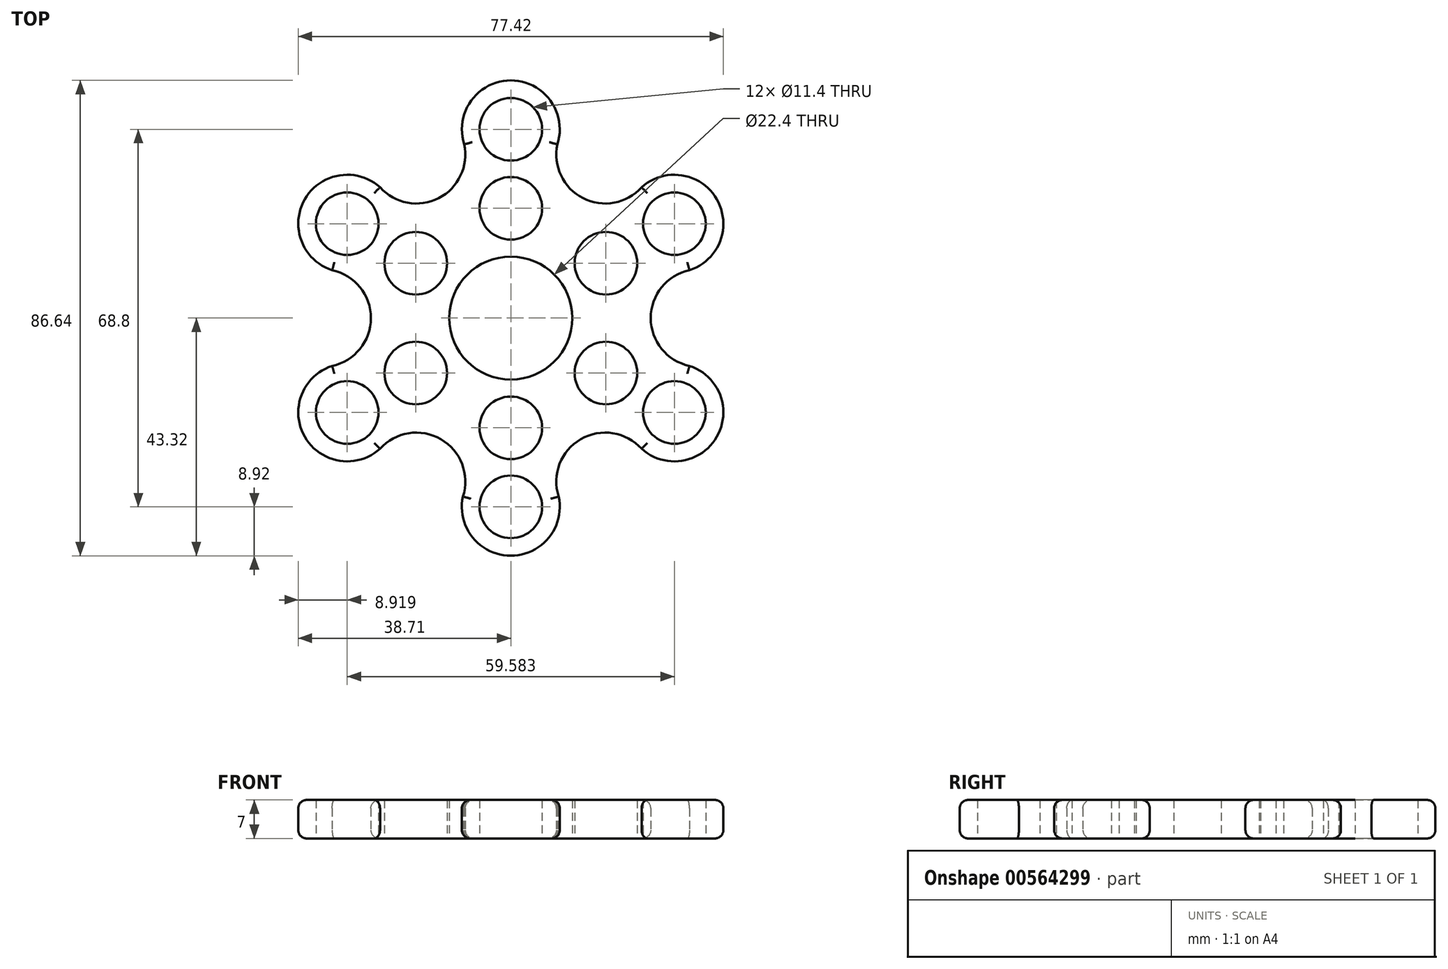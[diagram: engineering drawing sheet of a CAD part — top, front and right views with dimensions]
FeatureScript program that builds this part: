
annotation { "Feature Type Name" : "Feature", "Feature Type Description" : "" }
export const myFeature = defineFeature(function(context is Context, id is Id, definition is map)
    precondition{}
    {
        {
            var Q0;
            Q0=qCreatedBy(makeId("Top.planeOp"),FACE);
            var sketch = newSketch(context, id + "F0", { "sketchPlane" : qUnion([Q0])});
            skCircle(sketch, "E0", {"center": v(0, 0) * mm, "radius": 11.2 * mm});
            skCircle(sketch, "E1", {"center": v(0, 20) * mm, "radius": 5.7 * mm});
            skCircle(sketch, "E2", {"center": v(0, 34.4) * mm, "radius": 5.7 * mm});
            skArc(sketch, "E3", {"start": v(8.48, 31.66) * mm, "mid": v(0, 43.31) * mm, "end": v(-8.48, 31.66) * mm});
            skArc(sketch, "E4.1.0", {"start": v(-23.82, 23.82) * mm, "mid": v(-13.14, 21.85) * mm, "end": v(-8.48, 31.66) * mm});
            skArc(sketch, "E4.2.0", {"start": v(-23.82, 23.82) * mm, "mid": v(-37.51, 21.66) * mm, "end": v(-32.54, 8.72) * mm});
            skArc(sketch, "E4.3.0", {"start": v(-32.54, -8.72) * mm, "mid": v(-25.48, 0) * mm, "end": v(-32.54, 8.72) * mm});
            skArc(sketch, "E4.4.0", {"start": v(-32.54, -8.72) * mm, "mid": v(-37.51, -21.66) * mm, "end": v(-23.82, -23.82) * mm});
            skArc(sketch, "E4.5.0", {"start": v(-8.72, -32.54) * mm, "mid": v(-12.74, -22.07) * mm, "end": v(-23.82, -23.82) * mm});
            skArc(sketch, "E4.6.0", {"start": v(-8.72, -32.54) * mm, "mid": v(0, -43.31) * mm, "end": v(8.72, -32.54) * mm});
            skArc(sketch, "E4.7.0", {"start": v(23.82, -23.82) * mm, "mid": v(12.74, -22.07) * mm, "end": v(8.72, -32.54) * mm});
            skArc(sketch, "E4.8.0", {"start": v(23.82, -23.82) * mm, "mid": v(37.51, -21.66) * mm, "end": v(32.54, -8.72) * mm});
            skArc(sketch, "E4.9.0", {"start": v(32.54, 8.72) * mm, "mid": v(25.48, 0) * mm, "end": v(32.54, -8.72) * mm});
            skArc(sketch, "E4.10.0", {"start": v(32.54, 8.72) * mm, "mid": v(37.51, 21.66) * mm, "end": v(23.82, 23.82) * mm});
            skArc(sketch, "E4.11.0", {"start": v(8.48, 31.66) * mm, "mid": v(13.14, 21.85) * mm, "end": v(23.82, 23.82) * mm});
            skCircle(sketch, "E5.2.0", {"center": v(-29.8, 17.2) * mm, "radius": 5.7 * mm});
            skCircle(sketch, "E5.4.0", {"center": v(-29.8, -17.2) * mm, "radius": 5.7 * mm});
            skCircle(sketch, "E5.6.0", {"center": v(0, -34.4) * mm, "radius": 5.7 * mm});
            skCircle(sketch, "E5.8.0", {"center": v(29.8, -17.2) * mm, "radius": 5.7 * mm});
            skCircle(sketch, "E5.10.0", {"center": v(29.8, 17.2) * mm, "radius": 5.7 * mm});
            skCircle(sketch, "E6.1.0", {"center": v(-17.32, 10) * mm, "radius": 5.7 * mm});
            skCircle(sketch, "E6.2.0", {"center": v(-17.32, -10) * mm, "radius": 5.7 * mm});
            skCircle(sketch, "E6.3.0", {"center": v(0, -20) * mm, "radius": 5.7 * mm});
            skCircle(sketch, "E6.4.0", {"center": v(17.32, -10) * mm, "radius": 5.7 * mm});
            skCircle(sketch, "E6.5.0", {"center": v(17.32, 10) * mm, "radius": 5.7 * mm});
            skSolve(sketch);
        }
        {
            var Q0;
            Q0=makeQuery(id+"F0.imprint","IMPRINT",FACE,{"disambiguationData":[TD([[makeQuery(id+"F0.imprint","IMPRINT",EDGE,{"derivedFrom":sQuery(id+"F0.wireOp",EDGE,"E0")}),-1.0]])]});
            extrude(context, id + "F1", {"entities" : qUnion([Q0]), "depth" : 7 * mm, "offsetDistance" : 25 * mm});
        }
        {
            var Q0;
            Q0=makeQuery(id+"F1.opExtrude","CAP_EDGE",EDGE,{"disambiguationData":[OSD([sQuery(id+"F0.wireOp",EDGE,"E4.1.0")])],"isStart":false});
            var Q1;
            Q1=makeQuery(id+"F1.opExtrude","CAP_EDGE",EDGE,{"disambiguationData":[OSD([sQuery(id+"F0.wireOp",EDGE,"E3")])],"isStart":false});
            var Q2;
            Q2=makeQuery(id+"F1.opExtrude","CAP_EDGE",EDGE,{"disambiguationData":[OSD([sQuery(id+"F0.wireOp",EDGE,"E4.11.0")])],"isStart":false});
            var Q3;
            Q3=makeQuery(id+"F1.opExtrude","CAP_EDGE",EDGE,{"disambiguationData":[OSD([sQuery(id+"F0.wireOp",EDGE,"E4.10.0")])],"isStart":false});
            var Q4;
            Q4=makeQuery(id+"F1.opExtrude","CAP_EDGE",EDGE,{"disambiguationData":[OSD([sQuery(id+"F0.wireOp",EDGE,"E4.9.0")])],"isStart":false});
            var Q5;
            Q5=makeQuery(id+"F1.opExtrude","CAP_EDGE",EDGE,{"disambiguationData":[OSD([sQuery(id+"F0.wireOp",EDGE,"E4.8.0")])],"isStart":false});
            var Q6;
            Q6=makeQuery(id+"F1.opExtrude","CAP_EDGE",EDGE,{"disambiguationData":[OSD([sQuery(id+"F0.wireOp",EDGE,"E4.7.0")])],"isStart":false});
            var Q7;
            Q7=makeQuery(id+"F1.opExtrude","CAP_EDGE",EDGE,{"disambiguationData":[OSD([sQuery(id+"F0.wireOp",EDGE,"E4.6.0")])],"isStart":false});
            var Q8;
            Q8=makeQuery(id+"F1.opExtrude","CAP_EDGE",EDGE,{"disambiguationData":[OSD([sQuery(id+"F0.wireOp",EDGE,"E4.5.0")])],"isStart":false});
            var Q9;
            Q9=makeQuery(id+"F1.opExtrude","CAP_EDGE",EDGE,{"disambiguationData":[OSD([sQuery(id+"F0.wireOp",EDGE,"E4.4.0")])],"isStart":false});
            var Q10;
            Q10=makeQuery(id+"F1.opExtrude","CAP_EDGE",EDGE,{"disambiguationData":[OSD([sQuery(id+"F0.wireOp",EDGE,"E4.3.0")])],"isStart":false});
            var Q11;
            Q11=makeQuery(id+"F1.opExtrude","CAP_EDGE",EDGE,{"disambiguationData":[OSD([sQuery(id+"F0.wireOp",EDGE,"E4.2.0")])],"isStart":false});
            fillet(context, id + "F2", {"entities" : qUnion([Q0, Q1, Q2, Q3, Q4, Q5, Q6, Q7, Q8, Q9, Q10, Q11]), "radius" : 1.5 * mm, "tangentPropagation" : true, "allowEdgeOverflow" : false});
        }
        {
            var Q0;
            Q0=makeQuery(id+"F1.opExtrude","CAP_EDGE",EDGE,{"disambiguationData":[OSD([sQuery(id+"F0.wireOp",EDGE,"E4.4.0")])],"isStart":true});
            var Q1;
            Q1=makeQuery(id+"F1.opExtrude","CAP_EDGE",EDGE,{"disambiguationData":[OSD([sQuery(id+"F0.wireOp",EDGE,"E4.5.0")])],"isStart":true});
            var Q2;
            Q2=makeQuery(id+"F1.opExtrude","CAP_EDGE",EDGE,{"disambiguationData":[OSD([sQuery(id+"F0.wireOp",EDGE,"E4.6.0")])],"isStart":true});
            var Q3;
            Q3=makeQuery(id+"F1.opExtrude","CAP_EDGE",EDGE,{"disambiguationData":[OSD([sQuery(id+"F0.wireOp",EDGE,"E4.7.0")])],"isStart":true});
            var Q4;
            Q4=makeQuery(id+"F1.opExtrude","CAP_EDGE",EDGE,{"disambiguationData":[OSD([sQuery(id+"F0.wireOp",EDGE,"E4.8.0")])],"isStart":true});
            var Q5;
            Q5=makeQuery(id+"F1.opExtrude","CAP_EDGE",EDGE,{"disambiguationData":[OSD([sQuery(id+"F0.wireOp",EDGE,"E4.9.0")])],"isStart":true});
            var Q6;
            Q6=makeQuery(id+"F1.opExtrude","CAP_EDGE",EDGE,{"disambiguationData":[OSD([sQuery(id+"F0.wireOp",EDGE,"E4.10.0")])],"isStart":true});
            var Q7;
            Q7=makeQuery(id+"F1.opExtrude","CAP_EDGE",EDGE,{"disambiguationData":[OSD([sQuery(id+"F0.wireOp",EDGE,"E4.11.0")])],"isStart":true});
            var Q8;
            Q8=makeQuery(id+"F1.opExtrude","CAP_EDGE",EDGE,{"disambiguationData":[OSD([sQuery(id+"F0.wireOp",EDGE,"E3")])],"isStart":true});
            var Q9;
            Q9=makeQuery(id+"F1.opExtrude","CAP_EDGE",EDGE,{"disambiguationData":[OSD([sQuery(id+"F0.wireOp",EDGE,"E4.1.0")])],"isStart":true});
            var Q10;
            Q10=makeQuery(id+"F1.opExtrude","CAP_EDGE",EDGE,{"disambiguationData":[OSD([sQuery(id+"F0.wireOp",EDGE,"E4.2.0")])],"isStart":true});
            var Q11;
            Q11=makeQuery(id+"F1.opExtrude","CAP_EDGE",EDGE,{"disambiguationData":[OSD([sQuery(id+"F0.wireOp",EDGE,"E4.3.0")])],"isStart":true});
            fillet(context, id + "F3", {"entities" : qUnion([Q0, Q1, Q2, Q3, Q4, Q5, Q6, Q7, Q8, Q9, Q10, Q11]), "radius" : 1.5 * mm, "tangentPropagation" : true, "allowEdgeOverflow" : false});
        }
    });
